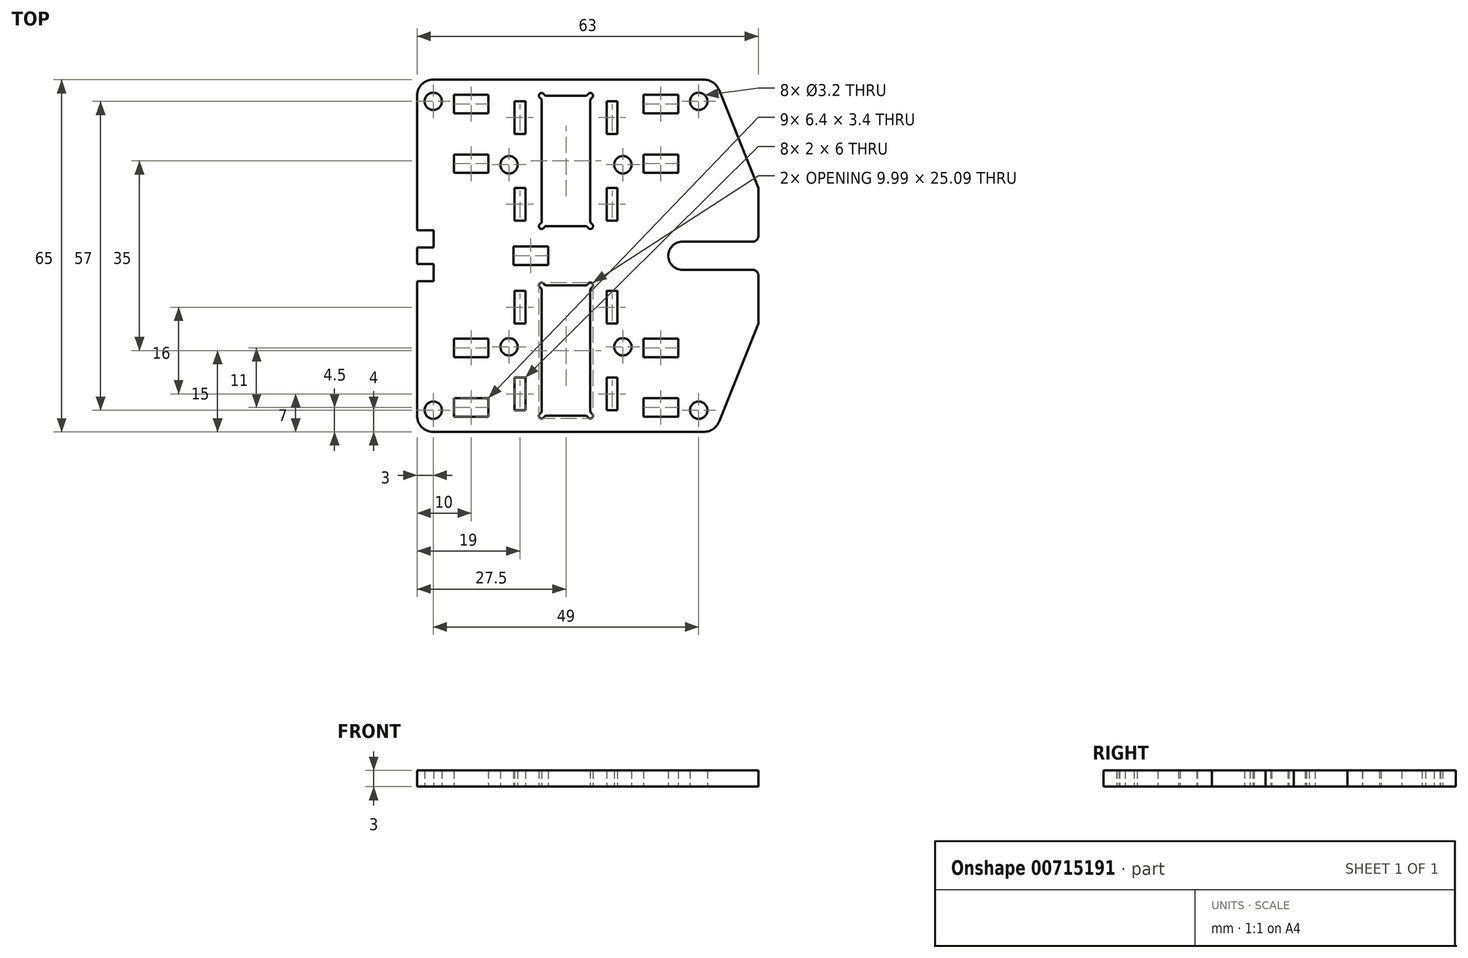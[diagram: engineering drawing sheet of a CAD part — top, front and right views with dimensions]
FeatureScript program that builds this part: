
annotation { "Feature Type Name" : "Feature", "Feature Type Description" : "" }
export const myFeature = defineFeature(function(context is Context, id is Id, definition is map)
    precondition{}
    {
        {
            var Q0;
            Q0=qCreatedBy(makeId("Top.planeOp"),FACE);
            var sketch = newSketch(context, id + "F0", { "sketchPlane" : qUnion([Q0])});
            skLineSegment(sketch, "E0", {"start": v(-31.5, -1.5) * mm, "end": v(-31.5, 1.5) * mm});
            skArc(sketch, "E1", {"start": v(-8.75, -29.12) * mm, "mid": v(-8.85, -29.9) * mm, "end": v(-8.07, -29.8) * mm});
            skArc(sketch, "E2", {"start": v(-7.63, -29.55) * mm, "mid": v(-7.88, -29.62) * mm, "end": v(-8.07, -29.8) * mm});
            skArc(sketch, "E3", {"start": v(-8.75, -29.12) * mm, "mid": v(-8.57, -28.93) * mm, "end": v(-8.5, -28.68) * mm});
            skLineSegment(sketch, "E4", {"start": v(-8.5, -6.32) * mm, "end": v(-8.5, -28.68) * mm});
            skArc(sketch, "E5", {"start": v(-8.5, -6.32) * mm, "mid": v(-8.57, -6.07) * mm, "end": v(-8.75, -5.88) * mm});
            skArc(sketch, "E6", {"start": v(-8.07, -5.2) * mm, "mid": v(-8.85, -5.1) * mm, "end": v(-8.75, -5.88) * mm});
            skArc(sketch, "E7", {"start": v(-8.07, -5.2) * mm, "mid": v(-7.88, -5.38) * mm, "end": v(-7.63, -5.45) * mm});
            skLineSegment(sketch, "E8", {"start": v(-0.37, -5.45) * mm, "end": v(-7.63, -5.45) * mm});
            skArc(sketch, "E9", {"start": v(-0.37, -5.45) * mm, "mid": v(-0.12, -5.38) * mm, "end": v(0.07, -5.2) * mm});
            skArc(sketch, "E10", {"start": v(0.75, -5.88) * mm, "mid": v(0.85, -5.1) * mm, "end": v(0.07, -5.2) * mm});
            skArc(sketch, "E11", {"start": v(0.75, -5.88) * mm, "mid": v(0.57, -6.07) * mm, "end": v(0.5, -6.32) * mm});
            skLineSegment(sketch, "E12", {"start": v(0.5, -28.68) * mm, "end": v(0.5, -6.32) * mm});
            skArc(sketch, "E13", {"start": v(0.5, -28.68) * mm, "mid": v(0.57, -28.93) * mm, "end": v(0.75, -29.12) * mm});
            skArc(sketch, "E14", {"start": v(0.07, -29.8) * mm, "mid": v(0.85, -29.9) * mm, "end": v(0.75, -29.12) * mm});
            skArc(sketch, "E15", {"start": v(0.07, -29.8) * mm, "mid": v(-0.12, -29.62) * mm, "end": v(-0.37, -29.55) * mm});
            skLineSegment(sketch, "E16", {"start": v(-7.63, -29.55) * mm, "end": v(-0.37, -29.55) * mm});
            skArc(sketch, "E17", {"start": v(-8.75, 5.88) * mm, "mid": v(-8.85, 5.1) * mm, "end": v(-8.07, 5.2) * mm});
            skArc(sketch, "E18", {"start": v(-7.63, 5.45) * mm, "mid": v(-7.88, 5.38) * mm, "end": v(-8.07, 5.2) * mm});
            skArc(sketch, "E19", {"start": v(-8.75, 5.88) * mm, "mid": v(-8.57, 6.07) * mm, "end": v(-8.5, 6.32) * mm});
            skLineSegment(sketch, "E20", {"start": v(-8.5, 28.68) * mm, "end": v(-8.5, 6.32) * mm});
            skArc(sketch, "E21", {"start": v(-8.5, 28.68) * mm, "mid": v(-8.57, 28.93) * mm, "end": v(-8.75, 29.12) * mm});
            skArc(sketch, "E22", {"start": v(-8.07, 29.8) * mm, "mid": v(-8.85, 29.9) * mm, "end": v(-8.75, 29.12) * mm});
            skArc(sketch, "E23", {"start": v(-8.07, 29.8) * mm, "mid": v(-7.88, 29.62) * mm, "end": v(-7.63, 29.55) * mm});
            skLineSegment(sketch, "E24", {"start": v(-0.37, 29.55) * mm, "end": v(-7.63, 29.55) * mm});
            skArc(sketch, "E25", {"start": v(-0.37, 29.55) * mm, "mid": v(-0.12, 29.62) * mm, "end": v(0.07, 29.8) * mm});
            skArc(sketch, "E26", {"start": v(0.75, 29.12) * mm, "mid": v(0.85, 29.9) * mm, "end": v(0.07, 29.8) * mm});
            skArc(sketch, "E27", {"start": v(0.75, 29.12) * mm, "mid": v(0.57, 28.93) * mm, "end": v(0.5, 28.68) * mm});
            skLineSegment(sketch, "E28", {"start": v(0.5, 6.32) * mm, "end": v(0.5, 28.68) * mm});
            skArc(sketch, "E29", {"start": v(0.5, 6.32) * mm, "mid": v(0.57, 6.07) * mm, "end": v(0.75, 5.88) * mm});
            skArc(sketch, "E30", {"start": v(0.07, 5.2) * mm, "mid": v(0.85, 5.1) * mm, "end": v(0.75, 5.88) * mm});
            skArc(sketch, "E31", {"start": v(0.07, 5.2) * mm, "mid": v(-0.12, 5.38) * mm, "end": v(-0.37, 5.45) * mm});
            skLineSegment(sketch, "E32", {"start": v(-7.63, 5.45) * mm, "end": v(-0.37, 5.45) * mm});
            skLineSegment(sketch, "E33", {"start": v(-31.5, -4.7) * mm, "end": v(-28.4, -4.7) * mm});
            skLineSegment(sketch, "E34", {"start": v(-28.4, -1.5) * mm, "end": v(-31.5, -1.5) * mm});
            skLineSegment(sketch, "E35", {"start": v(-28.4, -4.7) * mm, "end": v(-28.4, -1.5) * mm});
            skLineSegment(sketch, "E36", {"start": v(-31.5, 1.5) * mm, "end": v(-28.4, 1.5) * mm});
            skLineSegment(sketch, "E37", {"start": v(-28.4, 4.7) * mm, "end": v(-31.5, 4.7) * mm});
            skLineSegment(sketch, "E38", {"start": v(-28.4, 1.5) * mm, "end": v(-28.4, 4.7) * mm});
            skLineSegment(sketch, "E39", {"start": v(-13.7, 1.7) * mm, "end": v(-13.7, -1.7) * mm});
            skLineSegment(sketch, "E40", {"start": v(-13.7, -1.7) * mm, "end": v(-7.3, -1.7) * mm});
            skLineSegment(sketch, "E41", {"start": v(-13.7, 1.7) * mm, "end": v(-7.3, 1.7) * mm});
            skLineSegment(sketch, "E42", {"start": v(-7.3, -1.7) * mm, "end": v(-7.3, 1.7) * mm});
            skLineSegment(sketch, "E43", {"start": v(3.5, -12.5) * mm, "end": v(5.5, -12.5) * mm});
            skLineSegment(sketch, "E44", {"start": v(-13.5, -12.5) * mm, "end": v(-11.5, -12.5) * mm});
            skLineSegment(sketch, "E45", {"start": v(5.5, 12.5) * mm, "end": v(3.5, 12.5) * mm});
            skLineSegment(sketch, "E46", {"start": v(-11.5, 12.5) * mm, "end": v(-13.5, 12.5) * mm});
            skLineSegment(sketch, "E47", {"start": v(3.5, 22.5) * mm, "end": v(5.5, 22.5) * mm});
            skLineSegment(sketch, "E48", {"start": v(-13.5, 22.5) * mm, "end": v(-11.5, 22.5) * mm});
            skLineSegment(sketch, "E49", {"start": v(5.5, -22.5) * mm, "end": v(3.5, -22.5) * mm});
            skLineSegment(sketch, "E50", {"start": v(-11.5, -22.5) * mm, "end": v(-13.5, -22.5) * mm});
            skLineSegment(sketch, "E51", {"start": v(-13.5, -28.5) * mm, "end": v(-11.5, -28.5) * mm});
            skLineSegment(sketch, "E52", {"start": v(-11.5, -6.5) * mm, "end": v(-13.5, -6.5) * mm});
            skLineSegment(sketch, "E53", {"start": v(-13.5, 6.5) * mm, "end": v(-11.5, 6.5) * mm});
            skLineSegment(sketch, "E54", {"start": v(-11.5, 28.5) * mm, "end": v(-13.5, 28.5) * mm});
            skLineSegment(sketch, "E55", {"start": v(3.5, -28.5) * mm, "end": v(5.5, -28.5) * mm});
            skLineSegment(sketch, "E56", {"start": v(5.5, -6.5) * mm, "end": v(3.5, -6.5) * mm});
            skLineSegment(sketch, "E57", {"start": v(3.5, 6.5) * mm, "end": v(5.5, 6.5) * mm});
            skLineSegment(sketch, "E58", {"start": v(5.5, 28.5) * mm, "end": v(3.5, 28.5) * mm});
            skLineSegment(sketch, "E59", {"start": v(-13.5, -22.5) * mm, "end": v(-13.5, -28.5) * mm});
            skLineSegment(sketch, "E60", {"start": v(-11.5, -28.5) * mm, "end": v(-11.5, -22.5) * mm});
            skLineSegment(sketch, "E61", {"start": v(-13.5, -6.5) * mm, "end": v(-13.5, -12.5) * mm});
            skLineSegment(sketch, "E62", {"start": v(-11.5, -12.5) * mm, "end": v(-11.5, -6.5) * mm});
            skLineSegment(sketch, "E63", {"start": v(-13.5, 12.5) * mm, "end": v(-13.5, 6.5) * mm});
            skLineSegment(sketch, "E64", {"start": v(-11.5, 6.5) * mm, "end": v(-11.5, 12.5) * mm});
            skLineSegment(sketch, "E65", {"start": v(-13.5, 28.5) * mm, "end": v(-13.5, 22.5) * mm});
            skLineSegment(sketch, "E66", {"start": v(-11.5, 22.5) * mm, "end": v(-11.5, 28.5) * mm});
            skLineSegment(sketch, "E67", {"start": v(3.5, -22.5) * mm, "end": v(3.5, -28.5) * mm});
            skLineSegment(sketch, "E68", {"start": v(5.5, -28.5) * mm, "end": v(5.5, -22.5) * mm});
            skLineSegment(sketch, "E69", {"start": v(3.5, -6.5) * mm, "end": v(3.5, -12.5) * mm});
            skLineSegment(sketch, "E70", {"start": v(5.5, -12.5) * mm, "end": v(5.5, -6.5) * mm});
            skLineSegment(sketch, "E71", {"start": v(3.5, 12.5) * mm, "end": v(3.5, 6.5) * mm});
            skLineSegment(sketch, "E72", {"start": v(5.5, 6.5) * mm, "end": v(5.5, 12.5) * mm});
            skLineSegment(sketch, "E73", {"start": v(3.5, 28.5) * mm, "end": v(3.5, 22.5) * mm});
            skLineSegment(sketch, "E74", {"start": v(5.5, 22.5) * mm, "end": v(5.5, 28.5) * mm});
            skArc(sketch, "E75", {"start": v(17.5, 2.6) * mm, "mid": v(14.9, 0) * mm, "end": v(17.5, -2.6) * mm});
            skLineSegment(sketch, "E76", {"start": v(31.5, 12.5) * mm, "end": v(31.5, 3.6) * mm});
            skLineSegment(sketch, "E77", {"start": v(17.5, 2.6) * mm, "end": v(30.5, 2.6) * mm});
            skArc(sketch, "E78", {"start": v(30.5, 2.6) * mm, "mid": v(31.2, 2.9) * mm, "end": v(31.5, 3.6) * mm});
            skLineSegment(sketch, "E79", {"start": v(17.5, -2.6) * mm, "end": v(30.5, -2.6) * mm});
            skLineSegment(sketch, "E80", {"start": v(31.5, -12.5) * mm, "end": v(31.5, -3.6) * mm});
            skArc(sketch, "E81", {"start": v(31.5, -3.6) * mm, "mid": v(31.2, -2.9) * mm, "end": v(30.5, -2.6) * mm});
            skLineSegment(sketch, "E82", {"start": v(10.3, -26.3) * mm, "end": v(10.3, -29.7) * mm});
            skLineSegment(sketch, "E83", {"start": v(10.3, -29.7) * mm, "end": v(16.7, -29.7) * mm});
            skLineSegment(sketch, "E84", {"start": v(10.3, -26.3) * mm, "end": v(16.7, -26.3) * mm});
            skLineSegment(sketch, "E85", {"start": v(16.7, -29.7) * mm, "end": v(16.7, -26.3) * mm});
            skLineSegment(sketch, "E86", {"start": v(10.3, -15.3) * mm, "end": v(10.3, -18.7) * mm});
            skLineSegment(sketch, "E87", {"start": v(10.3, -18.7) * mm, "end": v(16.7, -18.7) * mm});
            skLineSegment(sketch, "E88", {"start": v(10.3, -15.3) * mm, "end": v(16.7, -15.3) * mm});
            skLineSegment(sketch, "E89", {"start": v(16.7, -18.7) * mm, "end": v(16.7, -15.3) * mm});
            skLineSegment(sketch, "E90", {"start": v(10.3, 18.7) * mm, "end": v(10.3, 15.3) * mm});
            skLineSegment(sketch, "E91", {"start": v(10.3, 15.3) * mm, "end": v(16.7, 15.3) * mm});
            skLineSegment(sketch, "E92", {"start": v(10.3, 18.7) * mm, "end": v(16.7, 18.7) * mm});
            skLineSegment(sketch, "E93", {"start": v(16.7, 15.3) * mm, "end": v(16.7, 18.7) * mm});
            skLineSegment(sketch, "E94", {"start": v(10.3, 29.7) * mm, "end": v(10.3, 26.3) * mm});
            skLineSegment(sketch, "E95", {"start": v(10.3, 26.3) * mm, "end": v(16.7, 26.3) * mm});
            skLineSegment(sketch, "E96", {"start": v(10.3, 29.7) * mm, "end": v(16.7, 29.7) * mm});
            skLineSegment(sketch, "E97", {"start": v(16.7, 26.3) * mm, "end": v(16.7, 29.7) * mm});
            skCircle(sketch, "E98", {"center": v(20.5, -28.5) * mm, "radius": 1.6 * mm});
            skCircle(sketch, "E99", {"center": v(20.5, 28.5) * mm, "radius": 1.6 * mm});
            skLineSegment(sketch, "E100", {"start": v(-24.7, -26.3) * mm, "end": v(-24.7, -29.7) * mm});
            skLineSegment(sketch, "E101", {"start": v(-24.7, -29.7) * mm, "end": v(-18.3, -29.7) * mm});
            skLineSegment(sketch, "E102", {"start": v(-24.7, -26.3) * mm, "end": v(-18.3, -26.3) * mm});
            skLineSegment(sketch, "E103", {"start": v(-18.3, -29.7) * mm, "end": v(-18.3, -26.3) * mm});
            skLineSegment(sketch, "E104", {"start": v(-24.7, -15.3) * mm, "end": v(-24.7, -18.7) * mm});
            skLineSegment(sketch, "E105", {"start": v(-24.7, -18.7) * mm, "end": v(-18.3, -18.7) * mm});
            skLineSegment(sketch, "E106", {"start": v(-24.7, -15.3) * mm, "end": v(-18.3, -15.3) * mm});
            skLineSegment(sketch, "E107", {"start": v(-18.3, -18.7) * mm, "end": v(-18.3, -15.3) * mm});
            skLineSegment(sketch, "E108", {"start": v(-24.7, 18.7) * mm, "end": v(-24.7, 15.3) * mm});
            skLineSegment(sketch, "E109", {"start": v(-24.7, 15.3) * mm, "end": v(-18.3, 15.3) * mm});
            skLineSegment(sketch, "E110", {"start": v(-24.7, 18.7) * mm, "end": v(-18.3, 18.7) * mm});
            skLineSegment(sketch, "E111", {"start": v(-18.3, 15.3) * mm, "end": v(-18.3, 18.7) * mm});
            skLineSegment(sketch, "E112", {"start": v(-24.7, 29.7) * mm, "end": v(-24.7, 26.3) * mm});
            skLineSegment(sketch, "E113", {"start": v(-24.7, 26.3) * mm, "end": v(-18.3, 26.3) * mm});
            skLineSegment(sketch, "E114", {"start": v(-24.7, 29.7) * mm, "end": v(-18.3, 29.7) * mm});
            skLineSegment(sketch, "E115", {"start": v(-18.3, 26.3) * mm, "end": v(-18.3, 29.7) * mm});
            skCircle(sketch, "E116", {"center": v(-28.5, -28.5) * mm, "radius": 1.6 * mm});
            skCircle(sketch, "E117", {"center": v(-28.5, 28.5) * mm, "radius": 1.6 * mm});
            skCircle(sketch, "E118", {"center": v(-14.5, -16.8) * mm, "radius": 1.6 * mm});
            skCircle(sketch, "E119", {"center": v(6.5, -16.8) * mm, "radius": 1.6 * mm});
            skCircle(sketch, "E120", {"center": v(6.5, 16.8) * mm, "radius": 1.6 * mm});
            skCircle(sketch, "E121", {"center": v(-14.5, 16.8) * mm, "radius": 1.6 * mm});
            skArc(sketch, "E122", {"start": v(24.25, 30.61) * mm, "mid": v(23.15, 31.98) * mm, "end": v(21.47, 32.5) * mm});
            skLineSegment(sketch, "E123", {"start": v(31.5, -12.5) * mm, "end": v(24.25, -30.61) * mm});
            skArc(sketch, "E124", {"start": v(21.47, -32.5) * mm, "mid": v(23.15, -31.98) * mm, "end": v(24.25, -30.61) * mm});
            skLineSegment(sketch, "E125", {"start": v(-31.5, -29.5) * mm, "end": v(-31.5, -4.7) * mm});
            skLineSegment(sketch, "E126", {"start": v(21.47, -32.5) * mm, "end": v(-28.5, -32.5) * mm});
            skArc(sketch, "E127", {"start": v(-31.5, -29.5) * mm, "mid": v(-30.62, -31.62) * mm, "end": v(-28.5, -32.5) * mm});
            skLineSegment(sketch, "E128", {"start": v(-31.5, 4.7) * mm, "end": v(-31.5, 29.5) * mm});
            skLineSegment(sketch, "E129", {"start": v(21.47, 32.5) * mm, "end": v(-28.5, 32.5) * mm});
            skArc(sketch, "E130", {"start": v(-28.5, 32.5) * mm, "mid": v(-30.62, 31.62) * mm, "end": v(-31.5, 29.5) * mm});
            skLineSegment(sketch, "E131", {"start": v(24.25, 30.61) * mm, "end": v(31.5, 12.5) * mm});
            skSolve(sketch);
        }
        {
            var Q0;
            Q0 = qSketchRegion(id + "F0", true);
            extrude(context, id + "F1", {"entities" : qUnion([Q0]), "depth" : 3 * mm, "offsetDistance" : 25 * mm});
        }
    });
